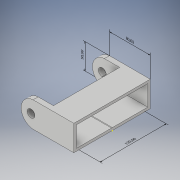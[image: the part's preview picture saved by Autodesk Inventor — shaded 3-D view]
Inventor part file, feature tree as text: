
AUTODESK INVENTOR PART (.ipt)
format: ipt  version: 2019 (Build 230136000, 136)  size: 163,840 bytes
history: native  units: mm
features: sketch x7, other x5, extrude x3, hole x3, plane x1, shell x1
ambient origin geometry x8: Origin, YZ Plane, XZ Plane, XY Plane, X Axis, Y Axis, Z Axis, Center Point
bodies: Body1 (feature_tree)
feature tree (20):
  other  "Sólido1"
  other  "Anotaciones"
  extrude  "Extrusión1"  Depth=150.0mm
  extrude  "Extrusión2"  Depth=50.0mm
  plane  "Plano de trabajo1"
  hole  "Agujero1"  [1 undecoded]
  extrude  "Extrusión3"  Depth=10.0mm TaperAngle=0.0deg
  hole  "Agujero2"  [1 undecoded]
  sketch  "Boceto6"  dims[d20=15.0mm d21=6.0mm d22=34.925mm d23=2.0mm d24=14.3117mm d25=8.0mm d26=20.594885mm d28=5.0mm]
  shell  "Vaciado1"  Thickness=130.0mm
  hole  "Agujero3"  [1 undecoded]
  sketch  "Boceto1"  dims[d0=50.0mm d1=150.0mm]
  sketch  "Boceto2"  dims[d2=50.0mm d3=0.0mm d4=30.0mm]
  sketch  "Boceto3"  dims[d5=30.0mm d6=10.0mm d7=0.0mm]
  sketch  "Boceto4"  dims[d10=-25.0mm]
  sketch  "Boceto5"  dims[d11=15.0mm d12=6.0mm d13=34.925mm d14=2.0mm d15=14.3117mm d16=8.0mm d17=20.594885mm d18=10.0mm d19=0.0mm]
  sketch  "Boceto7"  dims[d29=40.24mm d30=6.0mm d31=34.925mm d32=2.0mm d33=14.3117mm d34=8.0mm d35=20.594885mm d27=130.0mm d8=80.0mm d9=50.0mm]
  other  "Cota lineal 1"
  other  "Cota lineal 2"
  other  "Cota lineal 3"
note: 3 required parameter values undecoded (feature->parameter linkage not recoverable at this tier; creation-order binding heuristic only, values carry confidence <= 0.55)
